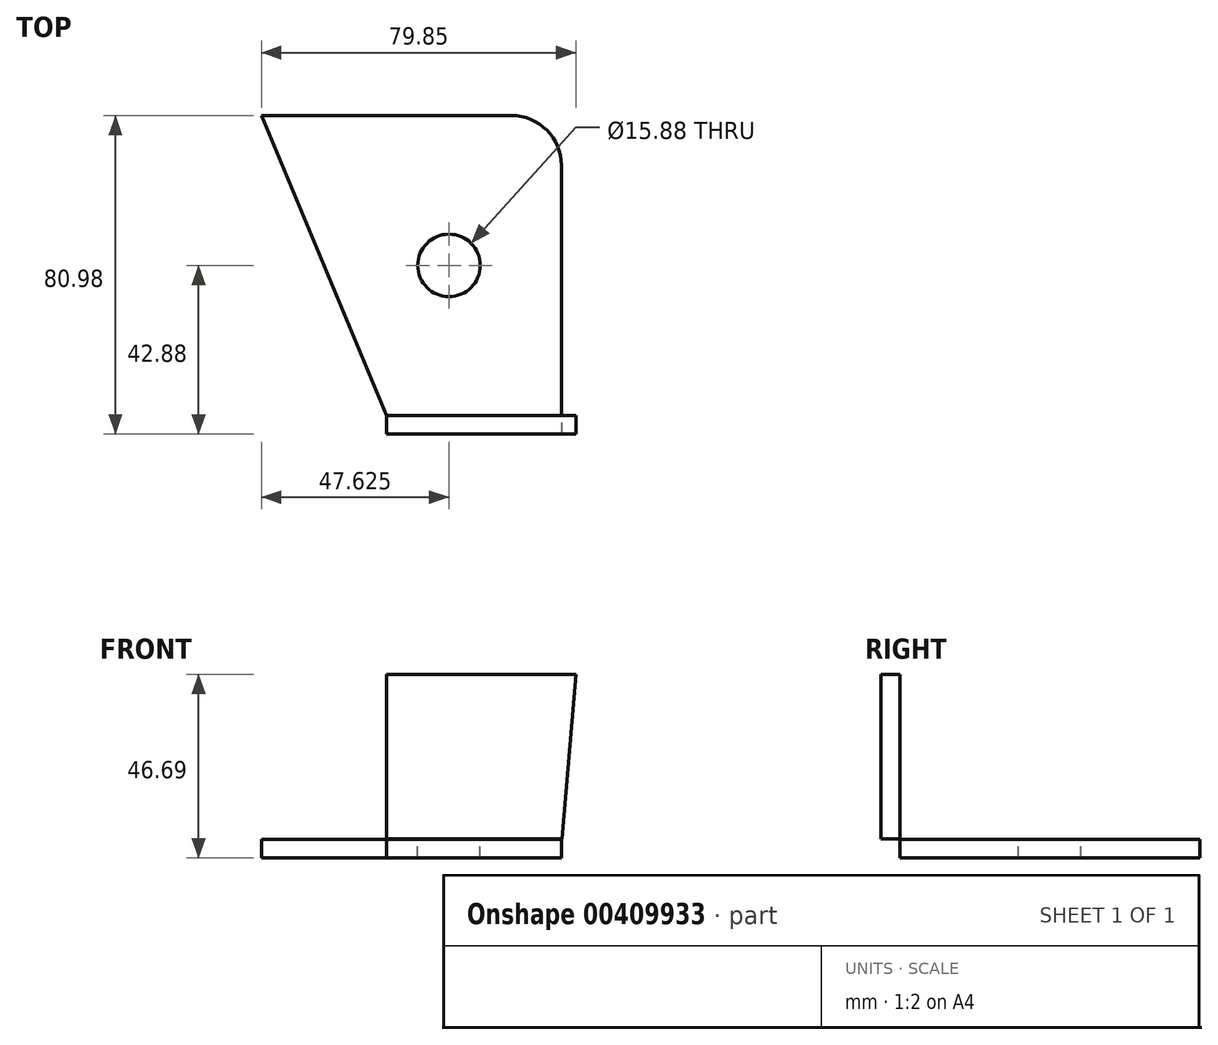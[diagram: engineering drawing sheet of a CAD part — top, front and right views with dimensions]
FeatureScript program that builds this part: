
annotation { "Feature Type Name" : "Feature", "Feature Type Description" : "" }
export const myFeature = defineFeature(function(context is Context, id is Id, definition is map)
    precondition{}
    {
        {
            var Q0;
            Q0=qCreatedBy(makeId("Top.planeOp"),FACE);
            var sketch = newSketch(context, id + "F0", { "sketchPlane" : qUnion([Q0])});
            skLineSegment(sketch, "E0", {"start": v(0, 0) * mm, "end": v(-31.75, 76.2) * mm});
            skLineSegment(sketch, "E1", {"start": v(-31.75, 76.2) * mm, "end": v(44.45, 76.2) * mm});
            skLineSegment(sketch, "E2", {"start": v(44.45, 76.2) * mm, "end": v(44.45, 0) * mm});
            skLineSegment(sketch, "E3", {"start": v(44.45, 0) * mm, "end": v(0, 0) * mm});
            skSolve(sketch);
        }
        {
            var Q0;
            Q0=makeQuery(id+"F0.imprint","IMPRINT",FACE,{"disambiguationData":[TD([[makeQuery(id+"F0.imprint","IMPRINT",EDGE,{"derivedFrom":sQuery(id+"F0.wireOp",EDGE,"E0")}),-1.0]])]});
            extrude(context, id + "F1", {"entities" : qUnion([Q0]), "depth" : 4.78 * mm});
        }
        {
            var Q0;
            Q0=makeQuery(id+"F1.opExtrude","SWEPT_EDGE",EDGE,{"disambiguationData":[OSD([sQuery(id+"F0.wireOp",EDGE,"E1"),sQuery(id+"F0.wireOp",EDGE,"E2")])]});
            fillet(context, id + "F2", {"entities" : qUnion([Q0]), "radius" : 12.7 * mm, "tangentPropagation" : true, "allowEdgeOverflow" : false});
        }
        {
            var Q0;
            Q0=makeQuery(id+"F1.opExtrude","CAP_FACE",FACE,{"disambiguationData":[OSD([sQuery(id+"F0.wireOp",EDGE,"E0"),sQuery(id+"F0.wireOp",EDGE,"E1"),sQuery(id+"F0.wireOp",EDGE,"E2"),sQuery(id+"F0.wireOp",EDGE,"E3")])],"isStart":false});
            var sketch = newSketch(context, id + "F3", { "sketchPlane" : qUnion([Q0])});
            skCircle(sketch, "E4", {"center": v(15.87, 38.1) * mm, "radius": 7.94 * mm});
            skSolve(sketch);
        }
        {
            var Q0;
            Q0=sQuery(id+"F3.wireOp",VERTEX,"E4.center");
            var Q1;
            Q1=makeQuery(id+"F1.opExtrude","SWEPT_BODY",BODY,{"disambiguationData":[OSD([sQuery(id+"F0.wireOp",EDGE,"E0"),sQuery(id+"F0.wireOp",EDGE,"E1"),sQuery(id+"F0.wireOp",EDGE,"E2"),sQuery(id+"F0.wireOp",EDGE,"E3")])]});
            hole(context, id + "F4", {"style" : HoleStyle.SIMPLE, "endStyle" : HoleEndStyle.THROUGH, "holeDiameter" : 15.88 * mm, "isTappedThrough" : true, "tappedDepth" : 12.7 * mm, "tapClearance" : 3, "locations" : qUnion([Q0]), "scope" : qUnion([Q1])});
        }
        {
            var Q0;
            Q0=qCreatedBy(makeId("Front.planeOp"),FACE);
            var sketch = newSketch(context, id + "F5", { "sketchPlane" : qUnion([Q0])});
            skLineSegment(sketch, "E5", {"start": v(0, 4.84) * mm, "end": v(0, 46.7) * mm});
            skLineSegment(sketch, "E6", {"start": v(0, 46.7) * mm, "end": v(48.1, 46.7) * mm});
            skLineSegment(sketch, "E7", {"start": v(48.1, 46.7) * mm, "end": v(44.6, 4.82) * mm});
            skLineSegment(sketch, "E8", {"start": v(44.6, 4.82) * mm, "end": v(0, 4.84) * mm});
            skSolve(sketch);
        }
        {
            var Q0;
            Q0=makeQuery(id+"F5.imprint","IMPRINT",FACE,{"disambiguationData":[TD([[makeQuery(id+"F5.imprint","IMPRINT",EDGE,{"derivedFrom":sQuery(id+"F5.wireOp",EDGE,"E5")}),-1.0]])]});
            extrude(context, id + "F6", {"entities" : qUnion([Q0]), "depth" : 4.78 * mm});
        }
    });
